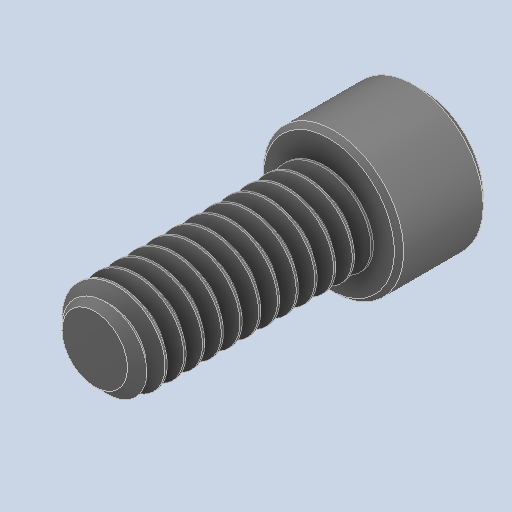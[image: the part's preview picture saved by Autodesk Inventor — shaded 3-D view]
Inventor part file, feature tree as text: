
AUTODESK INVENTOR PART (.ipt)
format: ipt  version: 2023.2 (Build 272271000, 271)  size: 538,112 bytes
history: native  units: in
note: dims shown in document units (in); Inventor stores cm internally (conversion verified against a paired STEP export)
features: chamfer x1
ambient origin geometry x8: Origin, YZ Plane, XZ Plane, XY Plane, X Axis, Y Axis, Z Axis, Center Point
bodies: Solid1 (feature_tree)
feature tree (1):
  chamfer  "Chamfer2"  [1 undecoded]
note: 1 required parameter value undecoded (feature->parameter linkage not recoverable at this tier; creation-order binding heuristic only, values carry confidence <= 0.55)
